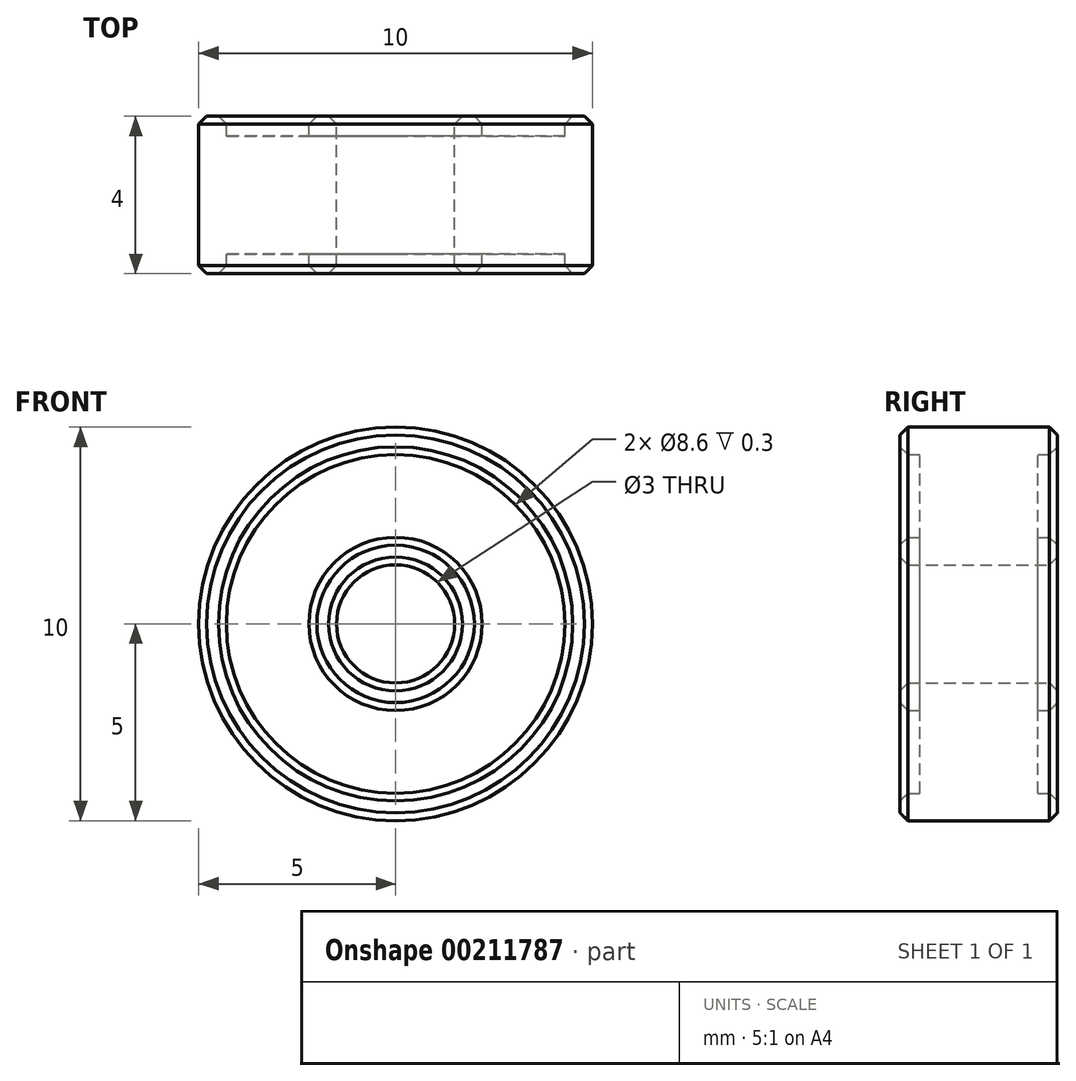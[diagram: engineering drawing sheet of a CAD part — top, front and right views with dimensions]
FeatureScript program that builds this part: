
annotation { "Feature Type Name" : "Feature", "Feature Type Description" : "" }
export const myFeature = defineFeature(function(context is Context, id is Id, definition is map)
    precondition{}
    {
        {
            var Q0;
            Q0=qCreatedBy(makeId("Front.planeOp"),FACE);
            var sketch = newSketch(context, id + "F0", { "sketchPlane" : qUnion([Q0])});
            skCircle(sketch, "E0", {"center": v(0, 0) * mm, "radius": 5 * mm});
            skCircle(sketch, "E1", {"center": v(0, 0) * mm, "radius": 4.3 * mm});
            skCircle(sketch, "E2", {"center": v(0, 0) * mm, "radius": 2.2 * mm});
            skCircle(sketch, "E3", {"center": v(0, 0) * mm, "radius": 1.5 * mm});
            skSolve(sketch);
        }
        {
            var Q0;
            Q0=makeQuery(id+"F0.imprint","IMPRINT",FACE,{"disambiguationData":[TD([[makeQuery(id+"F0.imprint","IMPRINT",EDGE,{"derivedFrom":sQuery(id+"F0.wireOp",EDGE,"E0")}),1.0]])]});
            var Q1;
            Q1=makeQuery(id+"F0.imprint","IMPRINT",FACE,{"disambiguationData":[TD([[makeQuery(id+"F0.imprint","IMPRINT",EDGE,{"derivedFrom":sQuery(id+"F0.wireOp",EDGE,"E2")}),1.0]])]});
            extrude(context, id + "F1", {"entities" : qUnion([Q0, Q1]), "endBound" : BoundingType.SYMMETRIC, "depth" : 4 * mm});
        }
        {
            var Q0;
            Q0=makeQuery(id+"F0.imprint","IMPRINT",FACE,{"disambiguationData":[TD([[makeQuery(id+"F0.imprint","IMPRINT",EDGE,{"derivedFrom":sQuery(id+"F0.wireOp",EDGE,"E1")}),1.0]])]});
            extrude(context, id + "F2", {"entities" : qUnion([Q0]), "operationType" : NewBodyOperationType.ADD, "endBound" : BoundingType.SYMMETRIC, "depth" : 3 * mm});
        }
        {
            var Q0;
            Q0=makeQuery(id+"F1.opExtrude","CAP_FACE",FACE,{"disambiguationData":[OSD([sQuery(id+"F0.wireOp",EDGE,"E0"),sQuery(id+"F0.wireOp",EDGE,"E1")])],"isStart":false});
            var Q1;
            Q1=makeQuery(id+"F1.opExtrude","CAP_FACE",FACE,{"disambiguationData":[OSD([sQuery(id+"F0.wireOp",EDGE,"E2"),sQuery(id+"F0.wireOp",EDGE,"E3")])],"isStart":false});
            var Q2;
            Q2=makeQuery(id+"F1.opExtrude","CAP_FACE",FACE,{"disambiguationData":[OSD([sQuery(id+"F0.wireOp",EDGE,"E0"),sQuery(id+"F0.wireOp",EDGE,"E1")])],"isStart":true});
            var Q3;
            Q3=makeQuery(id+"F1.opExtrude","CAP_FACE",FACE,{"disambiguationData":[OSD([sQuery(id+"F0.wireOp",EDGE,"E2"),sQuery(id+"F0.wireOp",EDGE,"E3")])],"isStart":true});
            chamfer(context, id + "F3", {"entities" : qUnion([Q0, Q1, Q2, Q3]), "width" : .2 * mm, "tangentPropagation" : true});
        }
    });
